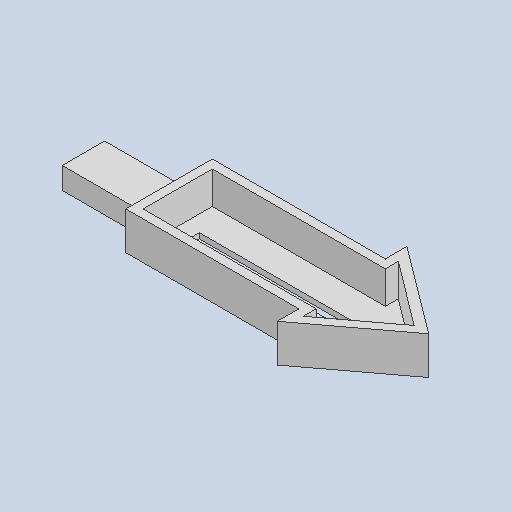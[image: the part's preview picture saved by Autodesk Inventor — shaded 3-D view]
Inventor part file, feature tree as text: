
AUTODESK INVENTOR PART (.ipt)
format: ipt  version: 2023 (Build 270158000, 158)  size: 313,344 bytes
history: native  units: in
note: dims shown in document units (in); Inventor stores cm internally (conversion verified against a paired STEP export)
features: extrude x5, sketch x5, projected_geometry x3
ambient origin geometry x8: Origin, YZ Plane, XZ Plane, XY Plane, X Axis, Y Axis, Z Axis, Center Point
bodies: Solid1 (feature_tree)
feature tree (13):
  extrude  "Extrusion1"  Depth=0.99in
  extrude  "Extrusion2"  Depth=0.495in
  extrude  "Extrusion3"  Depth=1.0in
  extrude  "Extrusion4"  Depth=0.0625in
  extrude  "Extrusion5"  Depth=0.375in
  sketch  "Sketch1"  dims[d0=0.49in d1=0.99in]
  sketch  "Sketch2"  dims[d2=0.245in d3=0.495in]
  projected_geometry  "Projected Loop1"
  sketch  "Sketch3"  dims[d4=0.25in d5=0.0in d6=1.0in]
  projected_geometry  "Projected Loop2"
  sketch  "Sketch4"  dims[d7=0.5in d8=0.0625in]
  projected_geometry  "Projected Loop3"
  sketch  "Sketch6"  dims[d9=2.0in d10=0.0in d11=1.5in d12=0.25in d13=0.5in d14=0.5in d15=1.0in d16=2.0in d17=2.0in d18=0.0625in d19=0.0in d20=0.1in d21=0.375in d22=0.0in d23=0.125in d24=0.0625in d25=0.375in d26=0.0in]
